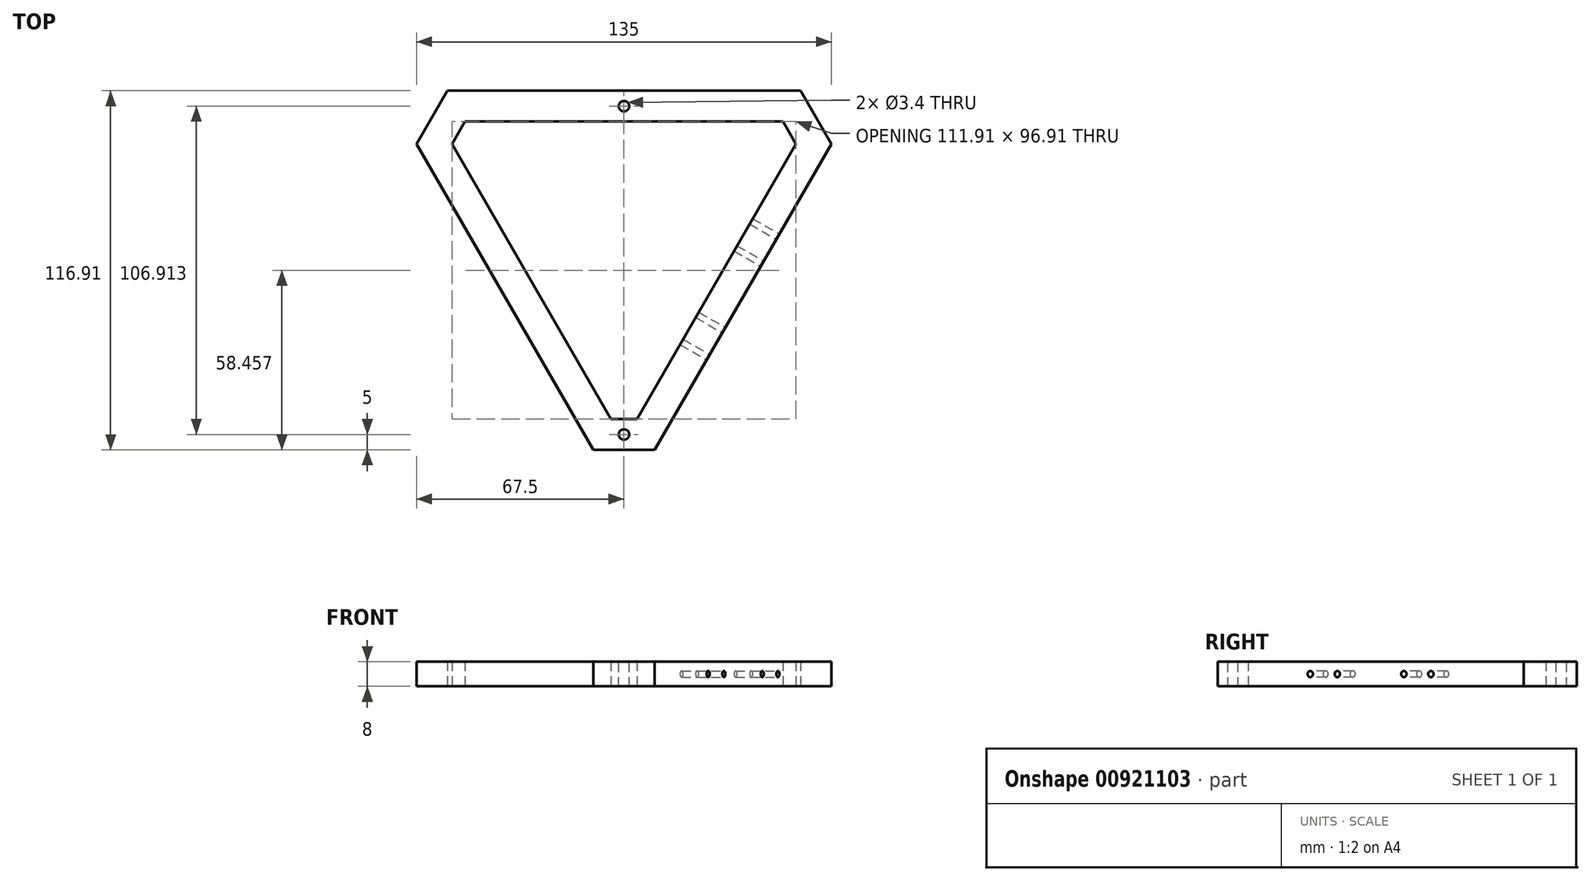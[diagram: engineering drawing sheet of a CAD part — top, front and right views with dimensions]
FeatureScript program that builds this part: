
annotation { "Feature Type Name" : "Feature", "Feature Type Description" : "" }
export const myFeature = defineFeature(function(context is Context, id is Id, definition is map)
    precondition{}
    {
        {
            var Q0;
            Q0=qCreatedBy(makeId("Top.planeOp"),FACE);
            var sketch = newSketch(context, id + "F0", { "sketchPlane" : qUnion([Q0])});
            skLineSegment(sketch, "E0", {"start": v(-57.5, 46.7) * mm, "end": v(57.5, 46.7) * mm});
            skLineSegment(sketch, "E1", {"start": v(57.5, 46.7) * mm, "end": v(67.5, 29.38) * mm});
            skLineSegment(sketch, "E2", {"start": v(67.5, 29.38) * mm, "end": v(10, -70.2) * mm});
            skLineSegment(sketch, "E3", {"start": v(10, -70.2) * mm, "end": v(-10, -70.2) * mm});
            skLineSegment(sketch, "E4", {"start": v(-10, -70.2) * mm, "end": v(-67.5, 29.38) * mm});
            skLineSegment(sketch, "E5", {"start": v(-67.5, 29.38) * mm, "end": v(-57.5, 46.7) * mm});
            skLineSegment(sketch, "E6", {"start": v(0, 46.7) * mm, "end": v(0, -70.2) * mm, "construction": true});
            skPoint(sketch, "E7", {"position": v(0, -11.75) * mm});
            skLineSegment(sketch, "E8.0", {"start": v(55.95, 29.38) * mm, "end": v(4.23, -60.2) * mm});
            skLineSegment(sketch, "E8.1", {"start": v(-4.23, -60.2) * mm, "end": v(-55.95, 29.38) * mm});
            skLineSegment(sketch, "E8.2", {"start": v(-55.95, 29.38) * mm, "end": v(-51.73, 36.7) * mm});
            skLineSegment(sketch, "E8.3", {"start": v(4.23, -60.2) * mm, "end": v(-4.23, -60.2) * mm});
            skLineSegment(sketch, "E8.4", {"start": v(-51.73, 36.7) * mm, "end": v(51.73, 36.7) * mm});
            skLineSegment(sketch, "E8.5", {"start": v(51.73, 36.7) * mm, "end": v(55.95, 29.38) * mm});
            skLineSegment(sketch, "E9", {"start": v(-38.75, -20.41) * mm, "end": v(62.5, 38.04) * mm, "construction": true});
            skLineSegment(sketch, "E10", {"start": v(38.75, -20.41) * mm, "end": v(-62.5, 38.04) * mm, "construction": true});
            skPoint(sketch, "E11", {"position": v(0, 1.96) * mm});
            skSolve(sketch);
        }
        {
            var Q0;
            Q0=qCreatedBy(makeId("Right.planeOp"),FACE);
            var sketch = newSketch(context, id + "F1", { "sketchPlane" : qUnion([Q0])});
            skLineSegment(sketch, "E12", {"start": v(2.08, 0) * mm, "end": v(2.08, 39.69) * mm, "construction": true});
            skSolve(sketch);
        }
        {
            var Q0;
            Q0 = qSketchRegion(id + "F0", true);
            extrude(context, id + "F2", {"entities" : qUnion([Q0]), "depth" : 8 * mm, "offsetDistance" : 25 * mm});
        }
        {
            var Q0;
            Q0=makeQuery(id+"F2.opExtrude","SWEPT_FACE",FACE,{"disambiguationData":[OSD([sQuery(id+"F0.wireOp",EDGE,"E2")])]});
            var sketch = newSketch(context, id + "F3", { "sketchPlane" : qUnion([Q0])});
            skLineSegment(sketch, "E13", {"start": v(-55.8, 4) * mm, "end": v(59.2, 4) * mm, "construction": true});
            skLineSegment(sketch, "E14", {"start": v(1.7, 8) * mm, "end": v(1.7, 0) * mm, "construction": true});
            skCircle(sketch, "E15", {"center": v(-10.8, 4) * mm, "radius": 1 * mm});
            skCircle(sketch, "E16", {"center": v(-20.97, 4) * mm, "radius": 1 * mm});
            skCircle(sketch, "E17.MirrorC", {"center": v(24.37, 4) * mm, "radius": 1 * mm});
            skCircle(sketch, "E18.MirrorC", {"center": v(14.2, 4) * mm, "radius": 1 * mm});
            skSolve(sketch);
        }
        {
            var Q0;
            Q0 = qSketchRegion(id + "F3", true);
            extrude(context, id + "F4", {"entities" : qUnion([Q0]), "operationType" : NewBodyOperationType.REMOVE, "oppositeDirection" : true, "depth" : 11 * mm, "offsetDistance" : 25 * mm});
        }
        {
            var Q0;
            Q0=makeQuery(id+"F2.opExtrude","CAP_FACE",FACE,{"disambiguationData":[OSD([sQuery(id+"F0.wireOp",EDGE,"E0"),sQuery(id+"F0.wireOp",EDGE,"E1"),sQuery(id+"F0.wireOp",EDGE,"E2"),sQuery(id+"F0.wireOp",EDGE,"E3"),sQuery(id+"F0.wireOp",EDGE,"E4"),sQuery(id+"F0.wireOp",EDGE,"E5"),sQuery(id+"F0.wireOp",EDGE,"E8.0"),sQuery(id+"F0.wireOp",EDGE,"E8.1"),sQuery(id+"F0.wireOp",EDGE,"E8.2"),sQuery(id+"F0.wireOp",EDGE,"E8.3"),sQuery(id+"F0.wireOp",EDGE,"E8.4"),sQuery(id+"F0.wireOp",EDGE,"E8.5")])],"isStart":false});
            var sketch = newSketch(context, id + "F5", { "sketchPlane" : qUnion([Q0])});
            skLineSegment(sketch, "E19", {"start": v(0, -60.2) * mm, "end": v(0, -70.2) * mm, "construction": true});
            skCircle(sketch, "E20", {"center": v(0, -65.2) * mm, "radius": 1.7 * mm});
            skSolve(sketch);
        }
        {
            var Q0;
            Q0 = qSketchRegion(id + "F5", true);
            extrude(context, id + "F6", {"entities" : qUnion([Q0]), "operationType" : NewBodyOperationType.REMOVE, "oppositeDirection" : true, "depth" : 10 * mm, "offsetDistance" : 25 * mm});
        }
        {
            var Q0;
            Q0=makeQuery(id+"F2.opExtrude","CAP_FACE",FACE,{"disambiguationData":[OSD([sQuery(id+"F0.wireOp",EDGE,"E0"),sQuery(id+"F0.wireOp",EDGE,"E1"),sQuery(id+"F0.wireOp",EDGE,"E2"),sQuery(id+"F0.wireOp",EDGE,"E3"),sQuery(id+"F0.wireOp",EDGE,"E4"),sQuery(id+"F0.wireOp",EDGE,"E5"),sQuery(id+"F0.wireOp",EDGE,"E8.0"),sQuery(id+"F0.wireOp",EDGE,"E8.1"),sQuery(id+"F0.wireOp",EDGE,"E8.2"),sQuery(id+"F0.wireOp",EDGE,"E8.3"),sQuery(id+"F0.wireOp",EDGE,"E8.4"),sQuery(id+"F0.wireOp",EDGE,"E8.5")])],"isStart":false});
            var sketch = newSketch(context, id + "F7", { "sketchPlane" : qUnion([Q0])});
            skLineSegment(sketch, "E21", {"start": v(0, 46.7) * mm, "end": v(0, 36.7) * mm, "construction": true});
            skCircle(sketch, "E22", {"center": v(0, 41.7) * mm, "radius": 1.7 * mm});
            skSolve(sketch);
        }
        {
            var Q0;
            Q0 = qSketchRegion(id + "F7", true);
            extrude(context, id + "F8", {"entities" : qUnion([Q0]), "operationType" : NewBodyOperationType.REMOVE, "oppositeDirection" : true, "depth" : 10 * mm, "offsetDistance" : 25 * mm});
        }
    });
